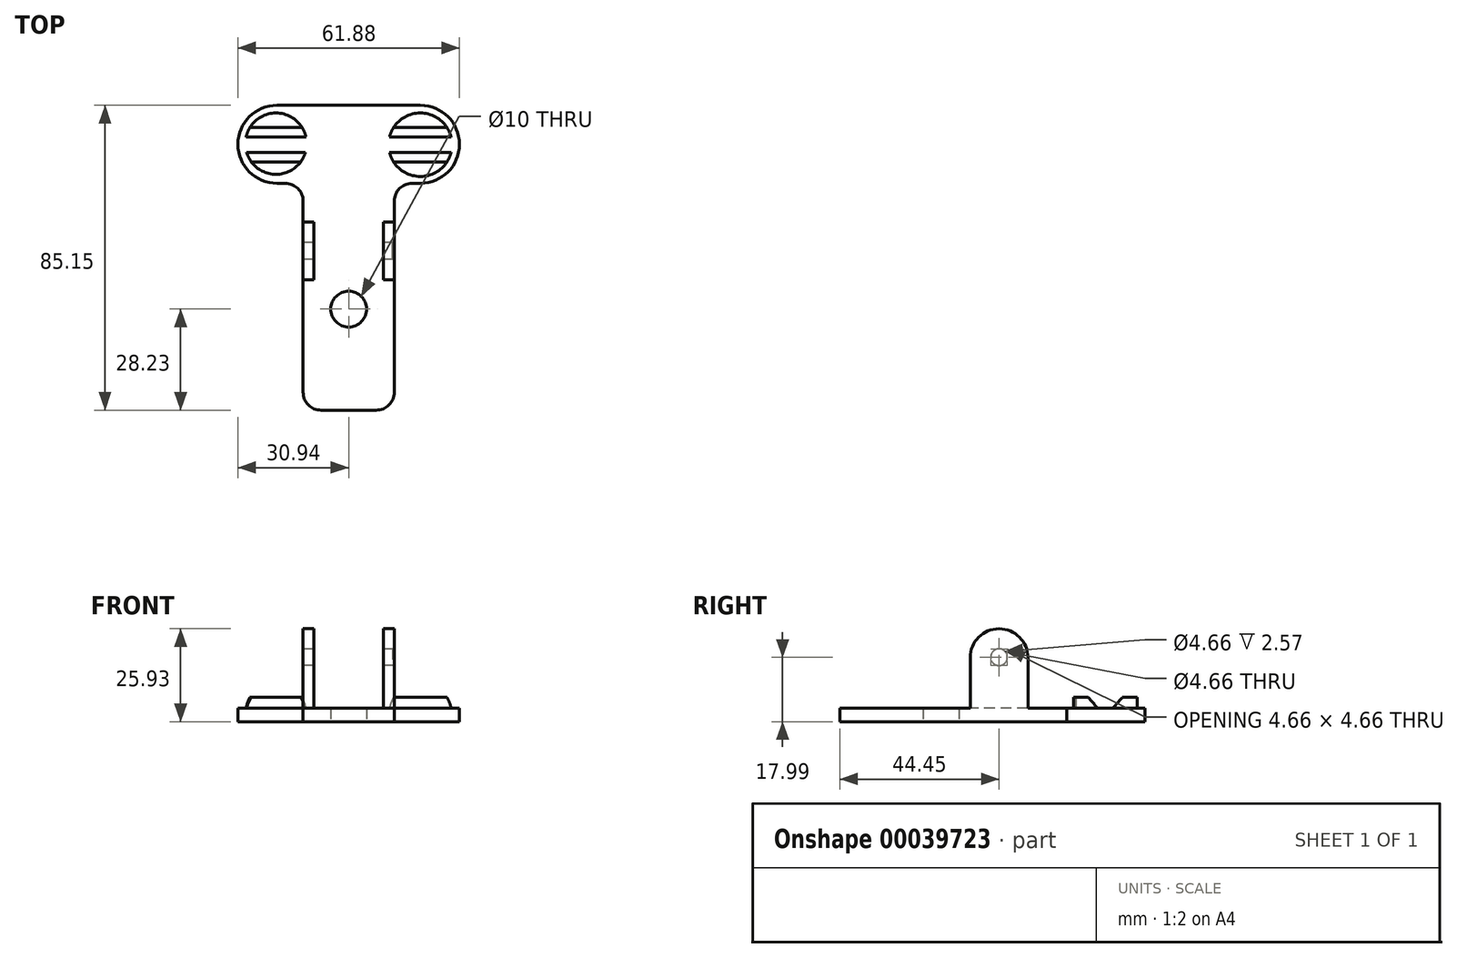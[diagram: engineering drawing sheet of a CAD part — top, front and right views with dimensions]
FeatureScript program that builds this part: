
annotation { "Feature Type Name" : "Feature", "Feature Type Description" : "" }
export const myFeature = defineFeature(function(context is Context, id is Id, definition is map)
    precondition{}
    {
        {
            var Q0;
            Q0=qCreatedBy(makeId("Top.planeOp"),FACE);
            var sketch = newSketch(context, id + "F0", { "sketchPlane" : qUnion([Q0])});
            skLineSegment(sketch, "E0.bottom", {"start": v(-12.72, 0) * mm, "end": v(12.72, 0) * mm});
            skLineSegment(sketch, "E0.top", {"start": v(-12.72, -63.35) * mm, "end": v(12.72, -63.35) * mm});
            skLineSegment(sketch, "E0.left", {"start": v(-12.72, 0) * mm, "end": v(-12.72, -63.35) * mm});
            skLineSegment(sketch, "E0.right", {"start": v(12.72, 0) * mm, "end": v(12.72, -63.35) * mm});
            skLineSegment(sketch, "E1.bottom", {"start": v(-30.93, 21.8) * mm, "end": v(30.93, 21.8) * mm});
            skLineSegment(sketch, "E1.top", {"start": v(-30.94, 0) * mm, "end": v(30.94, 0) * mm});
            skLineSegment(sketch, "E1.left", {"start": v(-30.94, 21.8) * mm, "end": v(-30.94, 0) * mm});
            skLineSegment(sketch, "E1.right", {"start": v(30.94, 21.8) * mm, "end": v(30.94, 0) * mm});
            skPoint(sketch, "E2", {"position": v(0, 0) * mm});
            skCircle(sketch, "E3", {"center": v(-20.3, 11.09) * mm, "radius": 8.56 * mm});
            skCircle(sketch, "E4", {"center": v(20, 10.79) * mm, "radius": 8.87 * mm});
            skCircle(sketch, "E5", {"center": v(0, -35.12) * mm, "radius": 5 * mm});
            skLineSegment(sketch, "E6", {"start": v(-28.51, 8.66) * mm, "end": v(-12.09, 8.66) * mm});
            skLineSegment(sketch, "E7", {"start": v(11.4, 8.66) * mm, "end": v(28.6, 8.66) * mm});
            skLineSegment(sketch, "E8", {"start": v(-28.67, 12.9) * mm, "end": v(-11.93, 12.91) * mm});
            skLineSegment(sketch, "E9", {"start": v(11.4, 12.91) * mm, "end": v(28.6, 12.91) * mm});
            skLineSegment(sketch, "E10", {"start": v(-27.6, 15.56) * mm, "end": v(-13, 15.56) * mm});
            skLineSegment(sketch, "E11", {"start": v(12.53, 15.56) * mm, "end": v(27.47, 15.56) * mm});
            skLineSegment(sketch, "E12", {"start": v(-27.6, 6.6) * mm, "end": v(-13, 6.61) * mm});
            skLineSegment(sketch, "E13", {"start": v(12.18, 6.61) * mm, "end": v(27.82, 6.61) * mm});
            skLineSegment(sketch, "E14.bottom", {"start": v(-12.72, -10.84) * mm, "end": v(-9.7, -10.84) * mm});
            skLineSegment(sketch, "E14.top", {"start": v(-12.72, -26.96) * mm, "end": v(-9.7, -26.96) * mm});
            skLineSegment(sketch, "E14.left", {"start": v(-12.72, -10.84) * mm, "end": v(-12.72, -26.96) * mm});
            skLineSegment(sketch, "E14.right", {"start": v(-9.7, -10.84) * mm, "end": v(-9.7, -26.96) * mm});
            skLineSegment(sketch, "E15.bottom", {"start": v(12.72, -10.84) * mm, "end": v(9.7, -10.84) * mm});
            skLineSegment(sketch, "E15.top", {"start": v(12.72, -26.96) * mm, "end": v(9.7, -26.96) * mm});
            skLineSegment(sketch, "E15.left", {"start": v(12.72, -10.84) * mm, "end": v(12.72, -26.96) * mm});
            skLineSegment(sketch, "E15.right", {"start": v(9.7, -10.84) * mm, "end": v(9.7, -26.96) * mm});
            skSolve(sketch);
        }
        {
            var Q0;
            Q0=makeQuery(id+"F0.imprint","IMPRINT",FACE,{"disambiguationData":[TD([[makeQuery(id+"F0.imprint","IMPRINT",EDGE,{"derivedFrom":sQuery(id+"F0.wireOp",EDGE,"E1.bottom")}),-1.0]])]});
            var Q1;
            {var subQ8=sQuery(id+"F0.wireOp",EDGE,"E0.top");Q1=makeQuery(id+"F0.imprint","IMPRINT",FACE,{"disambiguationData":[TD([[makeQuery(id+"F0.imprint","IMPRINT",EDGE,{"derivedFrom":subQ8}),1.0]])]});}
            var Q2;
            {var subQ0=sQuery(id+"F0.wireOp",EDGE,"E6");Q2=makeQuery(id+"F0.imprint","IMPRINT",FACE,{"disambiguationData":[TD([[makeQuery(id+"F0.imprint","IMPRINT",EDGE,{"derivedFrom":subQ0}),1.0]])]});}
            var Q3;
            {var subQ0=sQuery(id+"F0.wireOp",EDGE,"E7");Q3=makeQuery(id+"F0.imprint","IMPRINT",FACE,{"disambiguationData":[TD([[makeQuery(id+"F0.imprint","IMPRINT",EDGE,{"derivedFrom":subQ0}),1.0]])]});}
            extrude(context, id + "F1", {"entities" : qUnion([Q0, Q1, Q2, Q3]), "depth" : 3.75 * mm});
        }
        {
            var Q0;
            Q0=makeQuery(id+"F0.imprint","IMPRINT",FACE,{"disambiguationData":[TD([[makeQuery(id+"F0.imprint","IMPRINT",EDGE,{"derivedFrom":sQuery(id+"F0.wireOp",EDGE,"E14.bottom")}),-1.0]])]});
            var Q1;
            Q1=makeQuery(id+"F0.imprint","IMPRINT",FACE,{"disambiguationData":[TD([[makeQuery(id+"F0.imprint","IMPRINT",EDGE,{"derivedFrom":sQuery(id+"F0.wireOp",EDGE,"E15.bottom")}),1.0]])]});
            extrude(context, id + "F2", {"entities" : qUnion([Q0, Q1]), "operationType" : NewBodyOperationType.ADD, "depth" : 25.93 * mm});
        }
        {
            var Q0;
            {var subQ0=sQuery(id+"F0.wireOp",EDGE,"E10");Q0=makeQuery(id+"F0.imprint","IMPRINT",FACE,{"disambiguationData":[TD([[makeQuery(id+"F0.imprint","IMPRINT",EDGE,{"derivedFrom":subQ0}),1.0]])]});}
            var Q1;
            {var subQ0=sQuery(id+"F0.wireOp",EDGE,"E12");Q1=makeQuery(id+"F0.imprint","IMPRINT",FACE,{"disambiguationData":[TD([[makeQuery(id+"F0.imprint","IMPRINT",EDGE,{"derivedFrom":subQ0}),-1.0]])]});}
            var Q2;
            {var subQ0=sQuery(id+"F0.wireOp",EDGE,"E13");Q2=makeQuery(id+"F0.imprint","IMPRINT",FACE,{"disambiguationData":[TD([[makeQuery(id+"F0.imprint","IMPRINT",EDGE,{"derivedFrom":subQ0}),-1.0]])]});}
            var Q3;
            {var subQ0=sQuery(id+"F0.wireOp",EDGE,"E11");Q3=makeQuery(id+"F0.imprint","IMPRINT",FACE,{"disambiguationData":[TD([[makeQuery(id+"F0.imprint","IMPRINT",EDGE,{"derivedFrom":subQ0}),1.0]])]});}
            extrude(context, id + "F3", {"entities" : qUnion([Q0, Q1, Q2, Q3]), "operationType" : NewBodyOperationType.ADD, "depth" : 6.8 * mm});
        }
        {
            var Q0;
            {var subQ0=sQuery(id+"F0.wireOp",EDGE,"E8");Q0=makeQuery(id+"F0.imprint","IMPRINT",FACE,{"disambiguationData":[TD([[makeQuery(id+"F0.imprint","IMPRINT",EDGE,{"derivedFrom":subQ0}),1.0]])]});}
            var Q1;
            {var subQ0=sQuery(id+"F0.wireOp",EDGE,"E6");Q1=makeQuery(id+"F0.imprint","IMPRINT",FACE,{"disambiguationData":[TD([[makeQuery(id+"F0.imprint","IMPRINT",EDGE,{"derivedFrom":subQ0}),-1.0]])]});}
            var Q2;
            {var subQ0=sQuery(id+"F0.wireOp",EDGE,"E7");Q2=makeQuery(id+"F0.imprint","IMPRINT",FACE,{"disambiguationData":[TD([[makeQuery(id+"F0.imprint","IMPRINT",EDGE,{"derivedFrom":subQ0}),-1.0]])]});}
            var Q3;
            {var subQ0=sQuery(id+"F0.wireOp",EDGE,"E9");Q3=makeQuery(id+"F0.imprint","IMPRINT",FACE,{"disambiguationData":[TD([[makeQuery(id+"F0.imprint","IMPRINT",EDGE,{"derivedFrom":subQ0}),1.0]])]});}
            extrude(context, id + "F4", {"entities" : qUnion([Q0, Q1, Q2, Q3]), "operationType" : NewBodyOperationType.ADD, "depth" : 6.8 * mm});
        }
        {
            var Q0;
            Q0=makeQuery(id+"F4.opExtrude","CAP_EDGE",EDGE,{"disambiguationData":[OSD([sQuery(id+"F0.wireOp",EDGE,"E8")])],"isStart":false});
            var Q1;
            Q1=makeQuery(id+"F4.opExtrude","CAP_EDGE",EDGE,{"disambiguationData":[OSD([sQuery(id+"F0.wireOp",EDGE,"E9")])],"isStart":false});
            chamfer(context, id + "F5", {"entities" : qUnion([Q0, Q1]), "chamferType" : ChamferType.TWO_OFFSETS, "width1" : 2.65 * mm, "oppositeDirection" : false, "width2" : 3.04 * mm, "tangentPropagation" : true});
        }
        {
            var Q0;
            Q0=makeQuery(id+"F4.opExtrude","CAP_EDGE",EDGE,{"disambiguationData":[OSD([sQuery(id+"F0.wireOp",EDGE,"E6")])],"isStart":false});
            var Q1;
            Q1=makeQuery(id+"F4.opExtrude","CAP_EDGE",EDGE,{"disambiguationData":[OSD([sQuery(id+"F0.wireOp",EDGE,"E7")])],"isStart":false});
            chamfer(context, id + "F6", {"entities" : qUnion([Q0, Q1]), "chamferType" : ChamferType.TWO_OFFSETS, "width1" : 3.04 * mm, "oppositeDirection" : false, "width2" : 2.65 * mm, "tangentPropagation" : true});
        }
        {
            var Q0;
            {var subQ0=sQuery(id+"F0.wireOp",EDGE,"E14.left");var subQ1=sQuery(id+"F0.wireOp",EDGE,"E0.left");Q0=makeQuery(id+"F2.boolean.opBoolean","MERGE",FACE,{"derivedFrom":[makeQuery(id+"F1.opExtrude","SWEPT_FACE",FACE,{"disambiguationData":[OSD([subQ1]),TDD([makeQuery(id+"F0.imprint","IMPRINT",EDGE,{"disambiguationData":[TD([[makeQuery(id+"F0.imprint","INTERSECT",VERTEX,{"derivedFrom":[subQ1,sQuery(id+"F0.wireOp",EDGE,"E1.top")]}),-1.0]])],"derivedFrom":subQ1})])]}),makeQuery(id+"F1.opExtrude","SWEPT_FACE",FACE,{"disambiguationData":[OSD([subQ1]),TDD([makeQuery(id+"F0.imprint","IMPRINT",EDGE,{"disambiguationData":[TD([[makeQuery(id+"F0.imprint","INTERSECT",VERTEX,{"derivedFrom":[sQuery(id+"F0.wireOp",EDGE,"E0.top"),subQ1]}),1.0]])],"derivedFrom":subQ1})])]}),makeQuery(id+"F2.opExtrude","SWEPT_FACE",FACE,{"disambiguationData":[OSD([subQ0])]})]});}
            var sketch = newSketch(context, id + "F7", { "sketchPlane" : qUnion([Q0])});
            skCircle(sketch, "E16", {"center": v(18.9, 17.99) * mm, "radius": 2.33 * mm});
            skPoint(sketch, "E16.centerSnap0", {"position": v(18.9, 25.93) * mm});
            skSolve(sketch);
        }
        {
            var Q0;
            Q0=makeQuery(id+"F7.imprint","IMPRINT",FACE,{"disambiguationData":[TD([[makeQuery(id+"F7.imprint","IMPRINT",EDGE,{"derivedFrom":sQuery(id+"F7.wireOp",EDGE,"E16")}),1.0]])]});
            extrude(context, id + "F8", {"entities" : qUnion([Q0]), "operationType" : NewBodyOperationType.REMOVE, "oppositeDirection" : true, "depth" : 25 * mm});
        }
        {
            var Q0;
            Q0=makeQuery(id+"F2.opExtrude","CAP_EDGE",EDGE,{"disambiguationData":[OSD([sQuery(id+"F0.wireOp",EDGE,"E14.bottom")])],"isStart":false});
            var Q1;
            Q1=makeQuery(id+"F2.opExtrude","CAP_EDGE",EDGE,{"disambiguationData":[OSD([sQuery(id+"F0.wireOp",EDGE,"E15.bottom")])],"isStart":false});
            var Q2;
            Q2=makeQuery(id+"F2.opExtrude","CAP_EDGE",EDGE,{"disambiguationData":[OSD([sQuery(id+"F0.wireOp",EDGE,"E15.top")])],"isStart":false});
            var Q3;
            Q3=makeQuery(id+"F2.opExtrude","CAP_EDGE",EDGE,{"disambiguationData":[OSD([sQuery(id+"F0.wireOp",EDGE,"E14.top")])],"isStart":false});
            fillet(context, id + "F9", {"entities" : qUnion([Q0, Q1, Q2, Q3]), "radius" : 8.06 * mm, "tangentPropagation" : true, "allowEdgeOverflow" : false});
        }
        {
            var Q0;
            Q0=makeQuery(id+"F1.opExtrude","SWEPT_EDGE",EDGE,{"disambiguationData":[OSD([sQuery(id+"F0.wireOp",EDGE,"E0.left"),sQuery(id+"F0.wireOp",EDGE,"E1.top")])]});
            var Q1;
            Q1=makeQuery(id+"F1.opExtrude","SWEPT_EDGE",EDGE,{"disambiguationData":[OSD([sQuery(id+"F0.wireOp",EDGE,"E0.right"),sQuery(id+"F0.wireOp",EDGE,"E1.top")])]});
            var Q2;
            Q2=makeQuery(id+"F1.opExtrude","SWEPT_EDGE",EDGE,{"disambiguationData":[OSD([sQuery(id+"F0.wireOp",EDGE,"E0.top"),sQuery(id+"F0.wireOp",EDGE,"E0.right")])]});
            var Q3;
            Q3=makeQuery(id+"F1.opExtrude","SWEPT_EDGE",EDGE,{"disambiguationData":[OSD([sQuery(id+"F0.wireOp",EDGE,"E0.top"),sQuery(id+"F0.wireOp",EDGE,"E0.left")])]});
            var Q4;
            Q4=makeQuery(id+"F1.opExtrude","CAP_EDGE",EDGE,{"disambiguationData":[OSD([sQuery(id+"F0.wireOp",EDGE,"E14.top")])],"isStart":false});
            var Q5;
            Q5=makeQuery(id+"F1.opExtrude","CAP_EDGE",EDGE,{"disambiguationData":[OSD([sQuery(id+"F0.wireOp",EDGE,"E15.top")])],"isStart":false});
            var Q6;
            Q6=makeQuery(id+"F1.opExtrude","CAP_EDGE",EDGE,{"disambiguationData":[OSD([sQuery(id+"F0.wireOp",EDGE,"E15.bottom")])],"isStart":false});
            var Q7;
            Q7=makeQuery(id+"F1.opExtrude","CAP_EDGE",EDGE,{"disambiguationData":[OSD([sQuery(id+"F0.wireOp",EDGE,"E14.bottom")])],"isStart":false});
            fillet(context, id + "F10", {"entities" : qUnion([Q0, Q1, Q2, Q3, Q4, Q5, Q6, Q7]), "radius" : 5 * mm, "tangentPropagation" : true, "allowEdgeOverflow" : false});
        }
        {
            var Q0;
            Q0=makeQuery(id+"F1.opExtrude","SWEPT_EDGE",EDGE,{"disambiguationData":[OSD([sQuery(id+"F0.wireOp",EDGE,"E1.bottom"),sQuery(id+"F0.wireOp",EDGE,"E1.left")])]});
            var Q1;
            Q1=makeQuery(id+"F1.opExtrude","SWEPT_EDGE",EDGE,{"disambiguationData":[OSD([sQuery(id+"F0.wireOp",EDGE,"E1.top"),sQuery(id+"F0.wireOp",EDGE,"E1.left")])]});
            var Q2;
            Q2=makeQuery(id+"F1.opExtrude","SWEPT_EDGE",EDGE,{"disambiguationData":[OSD([sQuery(id+"F0.wireOp",EDGE,"E1.bottom"),sQuery(id+"F0.wireOp",EDGE,"E1.right")])]});
            var Q3;
            Q3=makeQuery(id+"F1.opExtrude","SWEPT_EDGE",EDGE,{"disambiguationData":[OSD([sQuery(id+"F0.wireOp",EDGE,"E1.top"),sQuery(id+"F0.wireOp",EDGE,"E1.right")])]});
            fillet(context, id + "F11", {"entities" : qUnion([Q0, Q1, Q2, Q3]), "radius" : 10.9 * mm, "tangentPropagation" : true, "allowEdgeOverflow" : false});
        }
    });
